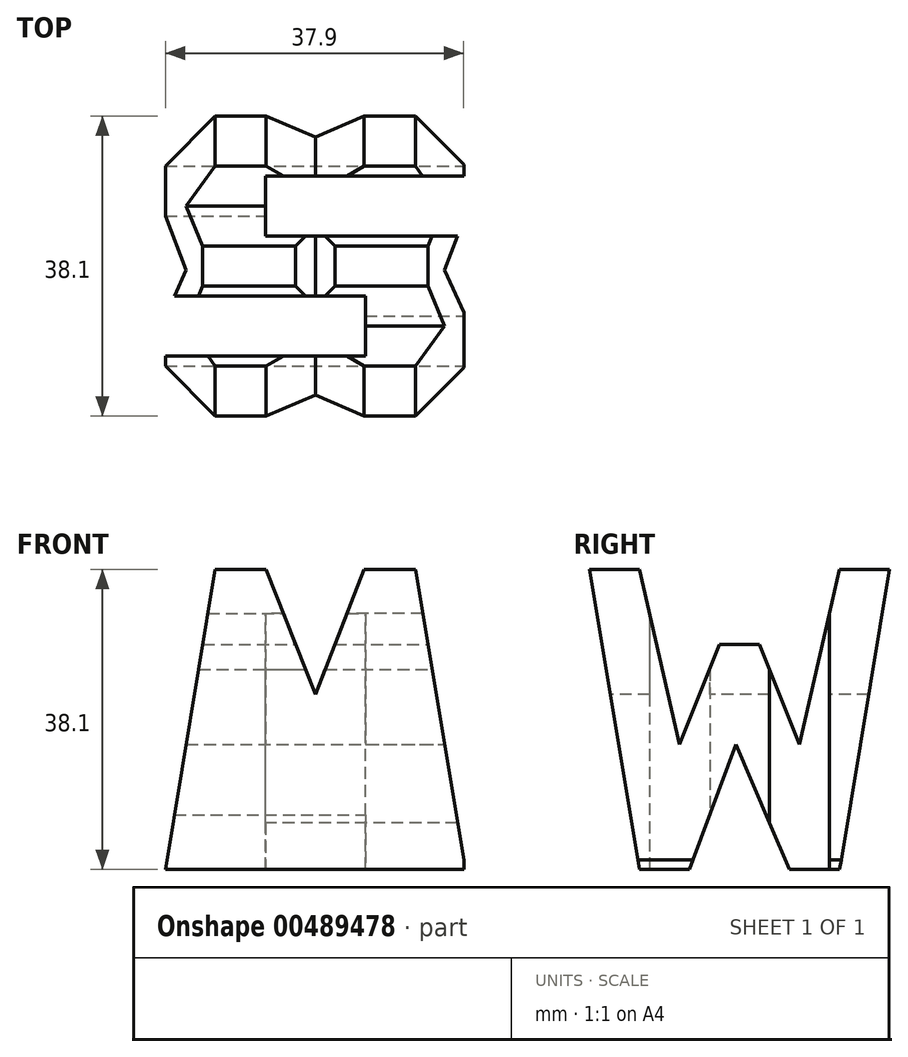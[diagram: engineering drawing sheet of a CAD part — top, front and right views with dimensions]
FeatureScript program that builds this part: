
annotation { "Feature Type Name" : "Feature", "Feature Type Description" : "" }
export const myFeature = defineFeature(function(context is Context, id is Id, definition is map)
    precondition{}
    {
        {
            var Q0;
            Q0=qCreatedBy(makeId("Front.planeOp"),FACE);
            var sketch = newSketch(context, id + "F0", { "sketchPlane" : qUnion([Q0])});
            skLineSegment(sketch, "E0", {"start": v(0, 0) * mm, "end": v(37.9, 0) * mm});
            skLineSegment(sketch, "E1", {"start": v(37.9, 0) * mm, "end": v(37.9, 38.1) * mm});
            skLineSegment(sketch, "E2", {"start": v(37.9, 38.1) * mm, "end": v(0, 38.1) * mm});
            skLineSegment(sketch, "E3", {"start": v(0, 38.1) * mm, "end": v(0, 0) * mm});
            skSolve(sketch);
        }
        {
            var Q0;
            Q0 = qSketchRegion(id + "F0", true);
            extrude(context, id + "F1", {"entities" : qUnion([Q0]), "depth" : 38.1 * mm, "offsetDistance" : 25.4 * mm});
        }
        {
            var Q0;
            Q0=qCreatedBy(makeId("Front.planeOp"),FACE);
            cPlane(context, id + "F2", {"entities" : qUnion([Q0]), "cplaneType" : CPlaneType.OFFSET, "offset" : 38.1 * mm, "width" : 152.4 * mm, "height" : 152.4 * mm});
        }
        {
            var Q0;
            Q0=qCreatedBy(makeId("Right.planeOp"),FACE);
            cPlane(context, id + "F3", {"entities" : qUnion([Q0]), "cplaneType" : CPlaneType.OFFSET, "offset" : 38.1 * mm, "width" : 152.4 * mm, "height" : 152.4 * mm});
        }
        {
            var Q0;
            Q0=qCreatedBy(makeId("Top.planeOp"),FACE);
            cPlane(context, id + "F4", {"entities" : qUnion([Q0]), "cplaneType" : CPlaneType.OFFSET, "offset" : 38.1 * mm, "width" : 152.4 * mm, "height" : 152.4 * mm});
        }
        {
            var Q0;
            Q0=qCreatedBy(id+"F3.planeOp",FACE);
            var sketch = newSketch(context, id + "F5", { "sketchPlane" : qUnion([Q0])});
            skLineSegment(sketch, "E4", {"start": v(-38.1, 38.1) * mm, "end": v(-38.1, 0) * mm});
            skLineSegment(sketch, "E5", {"start": v(-38.1, 0) * mm, "end": v(0, 0) * mm});
            skLineSegment(sketch, "E6", {"start": v(0, 0) * mm, "end": v(0, 38.1) * mm});
            skLineSegment(sketch, "E7", {"start": v(0, 38.1) * mm, "end": v(-38.1, 38.1) * mm});
            skLineSegment(sketch, "E8", {"start": v(-6.35, 38.1) * mm, "end": v(-11.43, 15.87) * mm});
            skLineSegment(sketch, "E9", {"start": v(0, 38.1) * mm, "end": v(-6.35, 0) * mm});
            skLineSegment(sketch, "E10", {"start": v(-31.75, 38.1) * mm, "end": v(-26.67, 15.88) * mm});
            skLineSegment(sketch, "E11", {"start": v(-38.1, 38.1) * mm, "end": v(-31.75, 0) * mm});
            skLineSegment(sketch, "E12", {"start": v(-11.43, 15.87) * mm, "end": v(-16.51, 28.58) * mm});
            skLineSegment(sketch, "E13", {"start": v(-16.51, 28.58) * mm, "end": v(-21.6, 28.58) * mm});
            skLineSegment(sketch, "E14", {"start": v(-21.6, 28.58) * mm, "end": v(-26.67, 15.88) * mm});
            skLineSegment(sketch, "E15", {"start": v(-19.54, 15.88) * mm, "end": v(-25.4, 0) * mm});
            skLineSegment(sketch, "E16", {"start": v(-19.54, 15.88) * mm, "end": v(-12.7, 0) * mm});
            skLineSegment(sketch, "E17", {"start": v(-38.1, 38.1) * mm, "end": v(0, 38.1) * mm});
            skSolve(sketch);
        }
        {
            var Q0;
            {var subQ1=sQuery(id+"F5.wireOp",EDGE,"E8");Q0=makeQuery(id+"F5.imprint","IMPRINT",FACE,{"disambiguationData":[TD([[makeQuery(id+"F5.imprint","IMPRINT",EDGE,{"derivedFrom":subQ1}),-1.0]])]});}
            var Q1;
            {var subQ0=sQuery(id+"F5.wireOp",EDGE,"E4");Q1=makeQuery(id+"F5.imprint","IMPRINT",FACE,{"disambiguationData":[TD([[makeQuery(id+"F5.imprint","IMPRINT",EDGE,{"derivedFrom":subQ0}),1.0]])]});}
            var Q2;
            {var subQ0=sQuery(id+"F5.wireOp",EDGE,"E15");Q2=makeQuery(id+"F5.imprint","IMPRINT",FACE,{"disambiguationData":[TD([[makeQuery(id+"F5.imprint","IMPRINT",EDGE,{"derivedFrom":subQ0}),1.0]])]});}
            var Q3;
            {var subQ0=sQuery(id+"F5.wireOp",EDGE,"E6");Q3=makeQuery(id+"F5.imprint","IMPRINT",FACE,{"disambiguationData":[TD([[makeQuery(id+"F5.imprint","IMPRINT",EDGE,{"derivedFrom":subQ0}),1.0]])]});}
            var Q4;
            Q4 = qSketchRegion(id + "F7", true);
            extrude(context, id + "F6", {"entities" : qUnion([Q0, Q1, Q2, Q3, Q4]), "operationType" : NewBodyOperationType.REMOVE, "oppositeDirection" : true, "depth" : 38.1 * mm, "offsetDistance" : 25.4 * mm});
        }
        {
            var Q0;
            Q0=qCreatedBy(id+"F2.planeOp",FACE);
            var sketch = newSketch(context, id + "F7", { "sketchPlane" : qUnion([Q0])});
            skLineSegment(sketch, "E18", {"start": v(0, 38.26) * mm, "end": v(0, 0) * mm});
            skLineSegment(sketch, "E19", {"start": v(0, 0) * mm, "end": v(31.75, 0) * mm});
            skLineSegment(sketch, "E20", {"start": v(12.7, 38.36) * mm, "end": v(19.05, 22.22) * mm});
            skLineSegment(sketch, "E21", {"start": v(19.05, 22.23) * mm, "end": v(25.4, 38.5) * mm});
            skLineSegment(sketch, "E22", {"start": v(26.67, 22.23) * mm, "end": v(31.75, 0) * mm});
            skLineSegment(sketch, "E23", {"start": v(31.75, 0) * mm, "end": v(26.67, 22.23) * mm});
            skLineSegment(sketch, "E24", {"start": v(26.67, 22.23) * mm, "end": v(21.59, 9.44) * mm});
            skLineSegment(sketch, "E25", {"start": v(21.59, 9.44) * mm, "end": v(16.51, 9.53) * mm});
            skLineSegment(sketch, "E26", {"start": v(16.51, 9.52) * mm, "end": v(11.43, 22.22) * mm});
            skLineSegment(sketch, "E27", {"start": v(11.43, 22.23) * mm, "end": v(6.35, 0) * mm});
            skLineSegment(sketch, "E28", {"start": v(31.75, 38.16) * mm, "end": v(38.1, 0) * mm});
            skLineSegment(sketch, "E29", {"start": v(38.1, 0) * mm, "end": v(38.1, 38.16) * mm});
            skLineSegment(sketch, "E30", {"start": v(38.1, 38.16) * mm, "end": v(0, 38.26) * mm});
            skLineSegment(sketch, "E31", {"start": v(0, 0) * mm, "end": v(6.35, 38.25) * mm});
            skLineSegment(sketch, "E32", {"start": v(31.75, 38.16) * mm, "end": v(31.75, 38.18) * mm});
            skSolve(sketch);
        }
        {
            var Q0;
            {var subQ0=sQuery(id+"F7.wireOp",EDGE,"E21");var subQ1=sQuery(id+"F7.wireOp",EDGE,"E20");var subQ2=makeQuery(id+"F7.imprint","INTERSECT",VERTEX,{"derivedFrom":[subQ1,subQ0]});Q0=makeQuery(id+"F7.imprint","IMPRINT",FACE,{"disambiguationData":[TD([[makeQuery(id+"F7.imprint","IMPRINT",EDGE,{"disambiguationData":[TD([[subQ2,1.0]])],"derivedFrom":subQ1}),1.0]])]});}
            var Q1;
            {var subQ0=sQuery(id+"F7.wireOp",EDGE,"E23");Q1=makeQuery(id+"F7.imprint","IMPRINT",FACE,{"disambiguationData":[TD([[makeQuery(id+"F7.imprint","IMPRINT",EDGE,{"derivedFrom":subQ0}),1.0]])]});}
            var Q2;
            Q2=makeQuery(id+"F7.imprint","IMPRINT",FACE,{"disambiguationData":[TD([[makeQuery(id+"F7.imprint","IMPRINT",EDGE,{"derivedFrom":sQuery(id+"F7.wireOp",EDGE,"E28")}),1.0]])]});
            var Q3;
            {var subQ0=sQuery(id+"F7.wireOp",EDGE,"E18");Q3=makeQuery(id+"F7.imprint","IMPRINT",FACE,{"disambiguationData":[TD([[makeQuery(id+"F7.imprint","IMPRINT",EDGE,{"derivedFrom":subQ0}),1.0]])]});}
            extrude(context, id + "F8", {"entities" : qUnion([Q0, Q1, Q2, Q3]), "operationType" : NewBodyOperationType.REMOVE, "oppositeDirection" : true, "depth" : 38.1 * mm, "offsetDistance" : 25.4 * mm});
        }
        {
            var Q0;
            Q0=qCreatedBy(id+"F4.planeOp",FACE);
            var sketch = newSketch(context, id + "F9", { "sketchPlane" : qUnion([Q0])});
            skLineSegment(sketch, "E33", {"start": v(0, 0) * mm, "end": v(0, -38.1) * mm});
            skLineSegment(sketch, "E34", {"start": v(0, -38.1) * mm, "end": v(38.1, -38.1) * mm});
            skLineSegment(sketch, "E35", {"start": v(38.1, -38.1) * mm, "end": v(38.1, 0) * mm});
            skLineSegment(sketch, "E36", {"start": v(38.1, 0) * mm, "end": v(0, 0) * mm});
            skLineSegment(sketch, "E37", {"start": v(38.1, -7.62) * mm, "end": v(12.7, -7.62) * mm});
            skLineSegment(sketch, "E38", {"start": v(12.7, -7.62) * mm, "end": v(12.7, -15.24) * mm});
            skLineSegment(sketch, "E39", {"start": v(12.7, -15.24) * mm, "end": v(38.1, -15.24) * mm});
            skLineSegment(sketch, "E40", {"start": v(0, -22.85) * mm, "end": v(25.4, -22.85) * mm});
            skLineSegment(sketch, "E41", {"start": v(25.4, -22.85) * mm, "end": v(25.4, -30.47) * mm});
            skLineSegment(sketch, "E42", {"start": v(25.4, -30.47) * mm, "end": v(0, -30.47) * mm});
            skSolve(sketch);
        }
        {
            var Q0;
            {var subQ0=sQuery(id+"F9.wireOp",EDGE,"E37");Q0=makeQuery(id+"F9.imprint","IMPRINT",FACE,{"disambiguationData":[TD([[makeQuery(id+"F9.imprint","IMPRINT",EDGE,{"derivedFrom":subQ0}),1.0]])]});}
            var Q1;
            {var subQ0=sQuery(id+"F9.wireOp",EDGE,"E40");Q1=makeQuery(id+"F9.imprint","IMPRINT",FACE,{"disambiguationData":[TD([[makeQuery(id+"F9.imprint","IMPRINT",EDGE,{"derivedFrom":subQ0}),-1.0]])]});}
            extrude(context, id + "F10", {"entities" : qUnion([Q0, Q1]), "operationType" : NewBodyOperationType.REMOVE, "oppositeDirection" : true, "depth" : 38.1 * mm, "offsetDistance" : 25.4 * mm});
        }
    });
